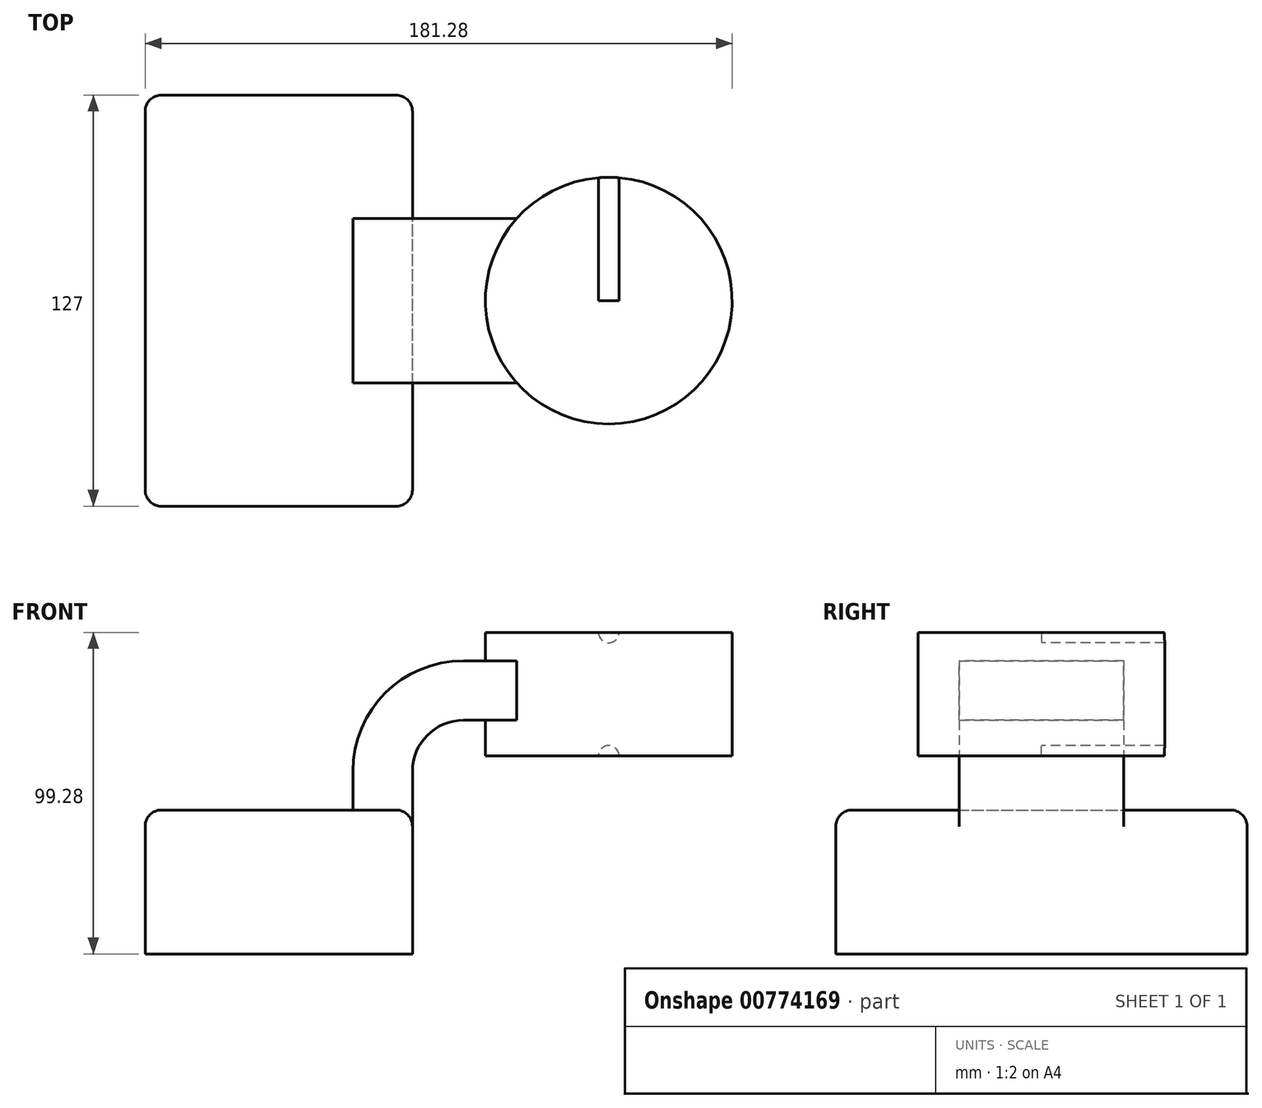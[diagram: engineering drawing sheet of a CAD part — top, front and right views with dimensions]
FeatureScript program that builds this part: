
annotation { "Feature Type Name" : "Feature", "Feature Type Description" : "" }
export const myFeature = defineFeature(function(context is Context, id is Id, definition is map)
    precondition{}
    {
        {
            var Q0;
            Q0=qCreatedBy(makeId("Front.planeOp"),FACE);
            var sketch = newSketch(context, id + "F0", { "sketchPlane" : qUnion([Q0])});
            skLineSegment(sketch, "E0.bottom", {"start": v(-41.27, 22.23) * mm, "end": v(41.27, 22.23) * mm});
            skLineSegment(sketch, "E0.top", {"start": v(-41.27, -22.23) * mm, "end": v(41.27, -22.23) * mm});
            skLineSegment(sketch, "E0.left", {"start": v(-41.27, 22.23) * mm, "end": v(-41.27, -22.23) * mm});
            skLineSegment(sketch, "E0.right", {"start": v(41.27, 22.23) * mm, "end": v(41.27, -22.23) * mm});
            skPoint(sketch, "E0.middle", {"position": v(0, 0) * mm});
            skLineSegment(sketch, "E1", {"start": v(41.27, 22.23) * mm, "end": v(41.27, 34.18) * mm});
            skArc(sketch, "E2", {"start": v(41.28, 34.18) * mm, "mid": v(45.89, 45.31) * mm, "end": v(57.02, 49.93) * mm});
            skLineSegment(sketch, "E3", {"start": v(57.02, 49.93) * mm, "end": v(101.58, 49.93) * mm});
            skLineSegment(sketch, "E4.0", {"start": v(57.02, 68.33) * mm, "end": v(101.58, 68.33) * mm});
            skArc(sketch, "E4.1", {"start": v(22.87, 34.18) * mm, "mid": v(32.87, 58.33) * mm, "end": v(57.02, 68.33) * mm});
            skLineSegment(sketch, "E4.2", {"start": v(22.87, 22.23) * mm, "end": v(22.87, 34.18) * mm});
            skFitSpline(sketch, "E5", {"points": [v(-41.28, 22.23) * mm, v(57.02, 68.33) * mm], "startDerivative": vector(4.04, 75.4) * mm, "endDerivative": vector(207.48, -0.85) * mm});
            skLineSegment(sketch, "E6", {"start": v(101.58, 68.33) * mm, "end": v(101.58, 49.93) * mm});
            skLineSegment(sketch, "E7.bottom", {"start": v(63.81, 77.05) * mm, "end": v(140.01, 77.05) * mm});
            skLineSegment(sketch, "E7.top", {"start": v(63.81, 38.95) * mm, "end": v(140.01, 38.95) * mm});
            skLineSegment(sketch, "E7.left", {"start": v(63.81, 77.05) * mm, "end": v(63.81, 38.95) * mm});
            skLineSegment(sketch, "E7.right", {"start": v(140.01, 77.05) * mm, "end": v(140.01, 38.95) * mm});
            skLineSegment(sketch, "E8", {"start": v(101.91, 77.05) * mm, "end": v(101.91, 38.95) * mm});
            skSolve(sketch);
        }
        {
            var Q0;
            Q0=makeQuery(id+"F0.imprint","IMPRINT",FACE,{"disambiguationData":[TD([[makeQuery(id+"F0.imprint","IMPRINT",EDGE,{"derivedFrom":sQuery(id+"F0.wireOp",EDGE,"E0.top")}),1.0]])]});
            extrude(context, id + "F1", {"entities" : qUnion([Q0]), "endBound" : BoundingType.SYMMETRIC, "depth" : 127 * mm, "offsetDistance" : 25.4 * mm});
        }
        {
            var Q0;
            Q0=makeQuery(id+"F0.imprint","IMPRINT",FACE,{"disambiguationData":[TD([[makeQuery(id+"F0.imprint","IMPRINT",EDGE,{"derivedFrom":sQuery(id+"F0.wireOp",EDGE,"E4.1")}),1.0]])]});
            extrude(context, id + "F2", {"entities" : qUnion([Q0]), "operationType" : NewBodyOperationType.ADD, "endBound" : BoundingType.SYMMETRIC, "depth" : 25.4 * mm, "offsetDistance" : 25.4 * mm});
        }
        {
            var Q0;
            {var subQ4=sQuery(id+"F0.wireOp",EDGE,"E1");Q0=makeQuery(id+"F0.imprint","IMPRINT",FACE,{"disambiguationData":[TD([[makeQuery(id+"F0.imprint","IMPRINT",EDGE,{"derivedFrom":subQ4}),1.0]])]});}
            var Q1;
            {var subQ0=sQuery(id+"F0.wireOp",EDGE,"E7.left");var subQ1=sQuery(id+"F0.wireOp",EDGE,"E3");var subQ2=makeQuery(id+"F0.imprint","INTERSECT",VERTEX,{"derivedFrom":[subQ1,subQ0]});Q1=makeQuery(id+"F0.imprint","IMPRINT",FACE,{"disambiguationData":[TD([[makeQuery(id+"F0.imprint","IMPRINT",EDGE,{"disambiguationData":[TD([[subQ2,-1.0]])],"derivedFrom":subQ1}),1.0]])]});}
            extrude(context, id + "F3", {"entities" : qUnion([Q0, Q1]), "operationType" : NewBodyOperationType.ADD, "endBound" : BoundingType.SYMMETRIC, "depth" : 50.8 * mm, "offsetDistance" : 25.4 * mm});
        }
        {
            var Q0;
            {var subQ0=sQuery(id+"F0.wireOp",EDGE,"E7.right");Q0=makeQuery(id+"F0.imprint","IMPRINT",FACE,{"disambiguationData":[TD([[makeQuery(id+"F0.imprint","IMPRINT",EDGE,{"derivedFrom":subQ0}),-1.0]])]});}
            var Q1;
            Q1=sQuery(id+"F0.wireOp",EDGE,"E8");
            revolve(context, id + "F4", {"operationType" : NewBodyOperationType.ADD, "surfaceOperationType" : NewSurfaceOperationType.NEW, "entities" : qUnion([Q0]), "axis" : qUnion([Q1]), "revolveType" : RevolveType.FULL});
        }
        {
            var Q0;
            Q0=makeQuery(id+"F1.opExtrude","CAP_EDGE",EDGE,{"disambiguationData":[OSD([sQuery(id+"F0.wireOp",EDGE,"E0.right")])],"isStart":false});
            var Q1;
            Q1=makeQuery(id+"F1.opExtrude","CAP_EDGE",EDGE,{"disambiguationData":[OSD([sQuery(id+"F0.wireOp",EDGE,"E0.right")])],"isStart":true});
            var Q2;
            Q2=makeQuery(id+"F1.opExtrude","CAP_EDGE",EDGE,{"disambiguationData":[OSD([sQuery(id+"F0.wireOp",EDGE,"E0.left")])],"isStart":true});
            var Q3;
            Q3=makeQuery(id+"F1.opExtrude","CAP_EDGE",EDGE,{"disambiguationData":[OSD([sQuery(id+"F0.wireOp",EDGE,"E0.left")])],"isStart":false});
            var Q4;
            Q4=makeQuery(id+"F1.opExtrude","CAP_EDGE",EDGE,{"disambiguationData":[OSD([sQuery(id+"F0.wireOp",EDGE,"E0.bottom")])],"isStart":false});
            var Q5;
            {var subQ0=sQuery(id+"F0.wireOp",EDGE,"E5");var subQ1=sQuery(id+"F0.wireOp",EDGE,"E0.bottom");var subQ2=sQuery(id+"F0.wireOp",EDGE,"E0.left");Q5=makeQuery(id+"F2.boolean.opBoolean","SPLIT",EDGE,{"disambiguationData":[TD([makeQuery(id+"F1.opExtrude","CAP_FACE",FACE,{"disambiguationData":[OSD([subQ1,sQuery(id+"F0.wireOp",EDGE,"E0.top"),subQ2,sQuery(id+"F0.wireOp",EDGE,"E0.right")])],"isStart":false})])],"derivedFrom":makeQuery(id+"F1.opExtrude","SWEPT_EDGE",EDGE,{"disambiguationData":[OSD([subQ1,subQ2,subQ0])]})});}
            var Q6;
            {var subQ0=sQuery(id+"F0.wireOp",EDGE,"E5");var subQ1=sQuery(id+"F0.wireOp",EDGE,"E0.bottom");var subQ2=sQuery(id+"F0.wireOp",EDGE,"E0.left");Q6=makeQuery(id+"F2.boolean.opBoolean","SPLIT",EDGE,{"disambiguationData":[TD([makeQuery(id+"F1.opExtrude","CAP_FACE",FACE,{"disambiguationData":[OSD([subQ1,sQuery(id+"F0.wireOp",EDGE,"E0.top"),subQ2,sQuery(id+"F0.wireOp",EDGE,"E0.right")])],"isStart":true})])],"derivedFrom":makeQuery(id+"F1.opExtrude","SWEPT_EDGE",EDGE,{"disambiguationData":[OSD([subQ1,subQ2,subQ0])]})});}
            var Q7;
            {var subQ0=sQuery(id+"F0.wireOp",EDGE,"E0.right");var subQ1=sQuery(id+"F0.wireOp",EDGE,"E0.bottom");var subQ2=sQuery(id+"F0.wireOp",EDGE,"E1");Q7=makeQuery(id+"F3.boolean.opBoolean","SPLIT",EDGE,{"disambiguationData":[TD([makeQuery(id+"F1.opExtrude","CAP_FACE",FACE,{"disambiguationData":[OSD([subQ1,sQuery(id+"F0.wireOp",EDGE,"E0.top"),sQuery(id+"F0.wireOp",EDGE,"E0.left"),subQ0])],"isStart":false})])],"derivedFrom":makeQuery(id+"F1.opExtrude","SWEPT_EDGE",EDGE,{"disambiguationData":[OSD([subQ1,subQ0,subQ2])]})});}
            var Q8;
            {var subQ0=sQuery(id+"F0.wireOp",EDGE,"E1");var subQ1=sQuery(id+"F0.wireOp",EDGE,"E0.bottom");var subQ2=sQuery(id+"F0.wireOp",EDGE,"E0.right");Q8=makeQuery(id+"F3.boolean.opBoolean","SPLIT",EDGE,{"disambiguationData":[TD([makeQuery(id+"F1.opExtrude","CAP_FACE",FACE,{"disambiguationData":[OSD([subQ1,sQuery(id+"F0.wireOp",EDGE,"E0.top"),sQuery(id+"F0.wireOp",EDGE,"E0.left"),subQ2])],"isStart":true})])],"derivedFrom":makeQuery(id+"F1.opExtrude","SWEPT_EDGE",EDGE,{"disambiguationData":[OSD([subQ1,subQ2,subQ0])]})});}
            var Q9;
            Q9=makeQuery(id+"F1.opExtrude","CAP_EDGE",EDGE,{"disambiguationData":[OSD([sQuery(id+"F0.wireOp",EDGE,"E0.bottom")])],"isStart":true});
            fillet(context, id + "F5", {"entities" : qUnion([Q0, Q1, Q2, Q3, Q4, Q5, Q6, Q7, Q8, Q9]), "radius" : 5.08 * mm, "tangentPropagation" : true, "allowEdgeOverflow" : false});
        }
        {
            var Q0;
            Q0=sQuery(id+"F0.wireOp",VERTEX,"E8.start");
            var Q1;
            Q1=sQuery(id+"F0.wireOp",VERTEX,"E8.end");
            var Q2;
            Q2=makeQuery(id+"F1.opExtrude","SWEPT_BODY",BODY,{"disambiguationData":[OSD([sQuery(id+"F0.wireOp",EDGE,"E0.bottom"),sQuery(id+"F0.wireOp",EDGE,"E0.top"),sQuery(id+"F0.wireOp",EDGE,"E0.left"),sQuery(id+"F0.wireOp",EDGE,"E0.right")])]});
            hole(context, id + "F6", {"style" : HoleStyle.SIMPLE, "endStyle" : HoleEndStyle.THROUGH, "holeDiameter" : 6.35 * mm, "majorDiameter" : 6.35 * mm, "isTappedThrough" : true, "tappedDepth" : 12.7 * mm, "tapClearance" : 3, "locations" : qUnion([Q0, Q1]), "scope" : qUnion([Q2])});
        }
    });
